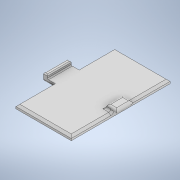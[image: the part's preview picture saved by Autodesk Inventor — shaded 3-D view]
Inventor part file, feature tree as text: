
AUTODESK INVENTOR PART (.ipt)
format: ipt  version: 2022 (Build 260153000, 153)  size: 175,104 bytes
history: native  units: mm
features: extrude x4, sketch x4, fillet x3, chamfer x1
ambient origin geometry x8: Origin, YZ Plane, XZ Plane, XY Plane, X Axis, Y Axis, Z Axis, Center Point
bodies: Solid1 (feature_tree)
feature tree (12):
  extrude  "Extrusion1"  Depth=50.0mm
  extrude  "Extrusion2"  Depth=4.0mm
  fillet  "Fillet1"  Radius=8.0mm
  extrude  "Extrusion3"  Depth=3.0mm
  extrude  "Extrusion4"  Depth=1.0mm
  fillet  "Fillet2"  Radius=6.0mm
  fillet  "Fillet3"  Radius=12.0mm
  chamfer  "Chamfer1"  Distance=5.0mm
  sketch  "Sketch1"  dims[d0=50.0mm d1=28.0mm]
  sketch  "Sketch2"  dims[d2=2.0mm d3=0.0mm d4=4.0mm d5=8.0mm]
  sketch  "Sketch3"  dims[d6=2.0mm d7=3.0mm]
  sketch  "Sketch4"  dims[d8=2.0mm d9=0.0mm d10=1.0mm d11=6.0mm d12=12.0mm d13=5.0mm d14=0.0mm d15=2.0mm d16=1.8mm d17=0.0mm d18=0.5mm d19=1.0mm d20=1.0mm d21=2.0mm d22=45.0deg]
